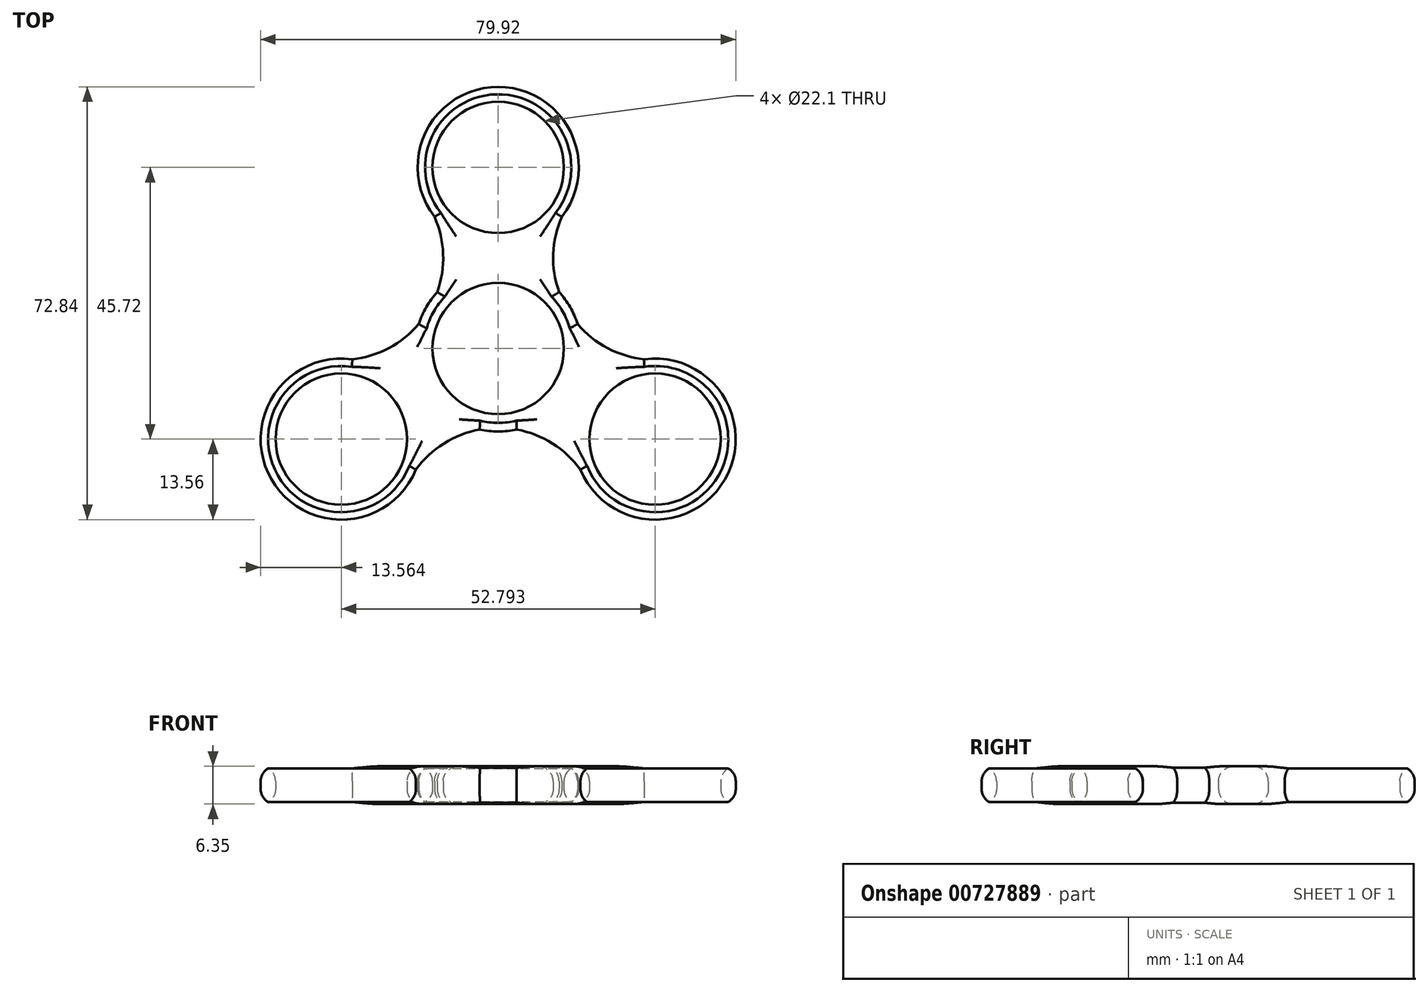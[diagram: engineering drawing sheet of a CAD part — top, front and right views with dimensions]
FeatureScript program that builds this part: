
annotation { "Feature Type Name" : "Feature", "Feature Type Description" : "" }
export const myFeature = defineFeature(function(context is Context, id is Id, definition is map)
    precondition{}
    {
        {
            var Q0;
            Q0=qCreatedBy(makeId("Top.planeOp"),FACE);
            var sketch = newSketch(context, id + "F0", { "sketchPlane" : qUnion([Q0])});
            skCircle(sketch, "E0", {"center": v(0, 0) * mm, "radius": 13.97 * mm});
            skCircle(sketch, "E1", {"center": v(0, 0) * mm, "radius": 11.05 * mm});
            skLineSegment(sketch, "E2", {"start": v(0, 0) * mm, "end": v(0, 30.48) * mm});
            skCircle(sketch, "E3", {"center": v(0, 30.48) * mm, "radius": 11.05 * mm});
            skCircle(sketch, "E4", {"center": v(0, 30.48) * mm, "radius": 13.56 * mm});
            skCircle(sketch, "E5.1.0", {"center": v(-26.4, -15.24) * mm, "radius": 11.05 * mm});
            skCircle(sketch, "E5.1.1", {"center": v(-26.4, -15.24) * mm, "radius": 13.56 * mm});
            skCircle(sketch, "E5.2.0", {"center": v(26.4, -15.24) * mm, "radius": 11.05 * mm});
            skCircle(sketch, "E5.2.1", {"center": v(26.4, -15.24) * mm, "radius": 13.56 * mm});
            skLineSegment(sketch, "E6", {"start": v(0, 0) * mm, "end": v(-26.4, 15.24) * mm});
            skArc(sketch, "E7", {"start": v(-28.24, -1.8) * mm, "mid": v(-11.55, 6.67) * mm, "end": v(-12.55, 25.36) * mm});
            skArc(sketch, "E8.1.0", {"start": v(15.68, -23.55) * mm, "mid": v(0, -13.33) * mm, "end": v(-15.68, -23.55) * mm});
            skArc(sketch, "E8.2.0", {"start": v(12.55, 25.36) * mm, "mid": v(11.55, 6.67) * mm, "end": v(28.24, -1.8) * mm});
            skSolve(sketch);
        }
        {
            var Q0;
            Q0 = qSketchRegion(id + "F0", true);
            extrude(context, id + "F1", {"entities" : qUnion([Q0]), "depth" : 6.35 * mm, "offsetDistance" : 25.4 * mm});
        }
        {
            var Q0;
            Q0=makeQuery(id+"F1.opExtrude","CAP_FACE",FACE,{"disambiguationData":[OSD([sQuery(id+"F0.wireOp",EDGE,"E0"),sQuery(id+"F0.wireOp",EDGE,"E1"),sQuery(id+"F0.wireOp",EDGE,"E3"),sQuery(id+"F0.wireOp",EDGE,"E4"),sQuery(id+"F0.wireOp",EDGE,"E5.1.0"),sQuery(id+"F0.wireOp",EDGE,"E5.1.1"),sQuery(id+"F0.wireOp",EDGE,"E5.2.0"),sQuery(id+"F0.wireOp",EDGE,"E5.2.1"),sQuery(id+"F0.wireOp",EDGE,"E7"),sQuery(id+"F0.wireOp",EDGE,"E8.1.0"),sQuery(id+"F0.wireOp",EDGE,"E8.2.0")])],"isStart":false});
            var Q1;
            Q1=makeQuery(id+"F1.opExtrude","CAP_FACE",FACE,{"disambiguationData":[OSD([sQuery(id+"F0.wireOp",EDGE,"E0"),sQuery(id+"F0.wireOp",EDGE,"E1"),sQuery(id+"F0.wireOp",EDGE,"E3"),sQuery(id+"F0.wireOp",EDGE,"E4"),sQuery(id+"F0.wireOp",EDGE,"E5.1.0"),sQuery(id+"F0.wireOp",EDGE,"E5.1.1"),sQuery(id+"F0.wireOp",EDGE,"E5.2.0"),sQuery(id+"F0.wireOp",EDGE,"E5.2.1"),sQuery(id+"F0.wireOp",EDGE,"E7"),sQuery(id+"F0.wireOp",EDGE,"E8.1.0"),sQuery(id+"F0.wireOp",EDGE,"E8.2.0")])],"isStart":true});
            fillet(context, id + "F2", {"entities" : qUnion([Q0, Q1]), "radius" : 2.54 * mm, "tangentPropagation" : true, "allowEdgeOverflow" : false});
        }
    });
